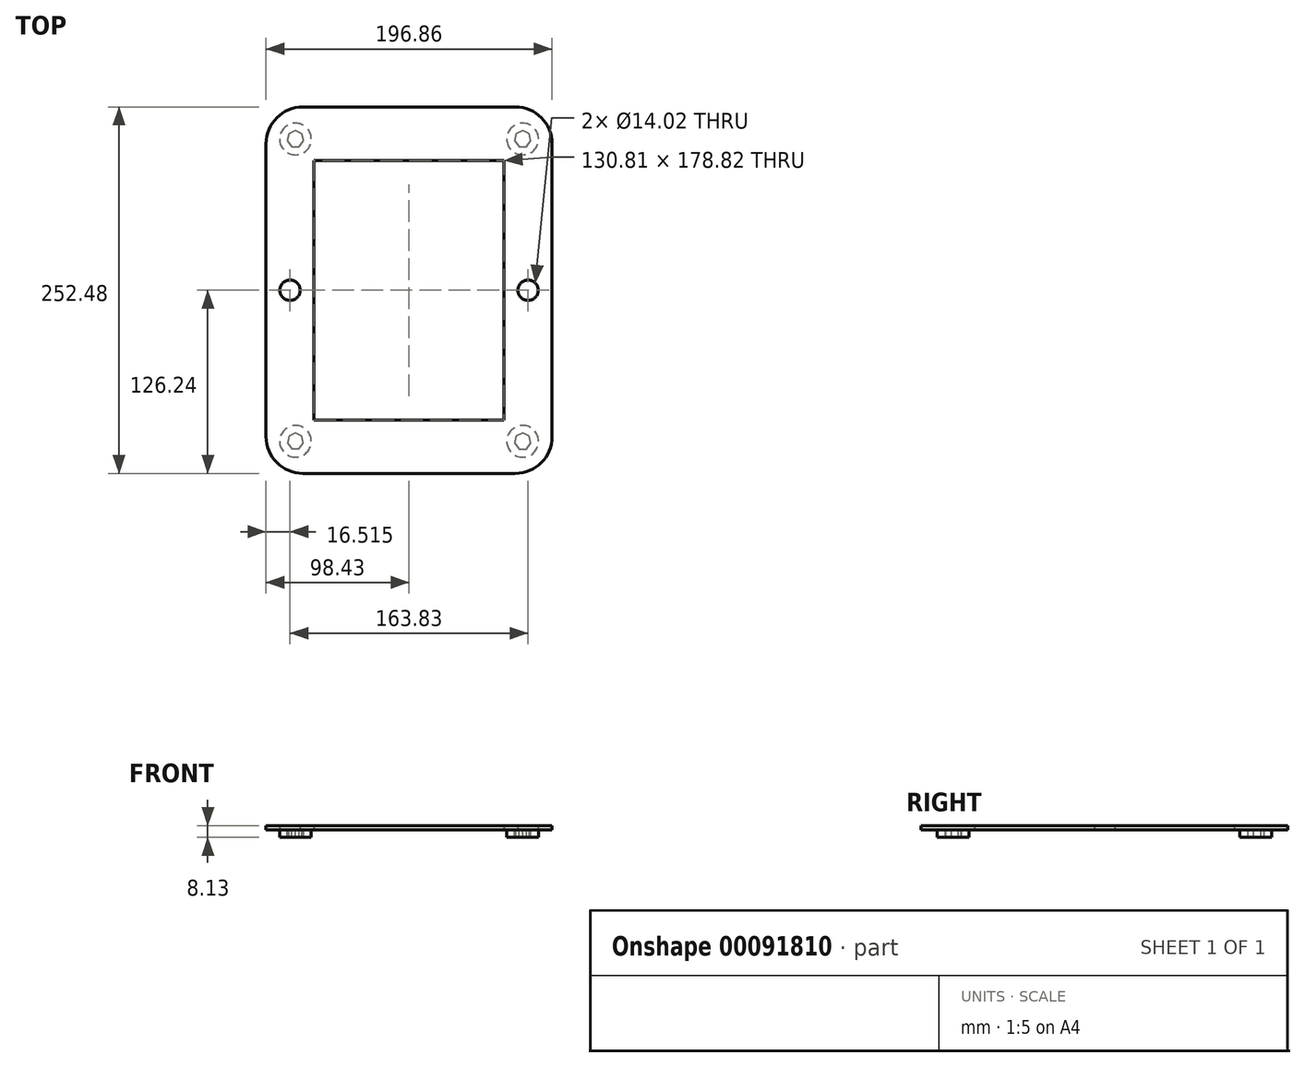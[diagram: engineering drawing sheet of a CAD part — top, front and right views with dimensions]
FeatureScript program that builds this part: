
annotation { "Feature Type Name" : "Feature", "Feature Type Description" : "" }
export const myFeature = defineFeature(function(context is Context, id is Id, definition is map)
    precondition{}
    {
        {
            var Q0;
            Q0=qCreatedBy(makeId("Top.planeOp"),FACE);
            var sketch = newSketch(context, id + "F0", { "sketchPlane" : qUnion([Q0])});
            skLineSegment(sketch, "E0.bottom", {"start": v(-73.02, -126.24) * mm, "end": v(73.03, -126.24) * mm});
            skLineSegment(sketch, "E0.top", {"start": v(-73.03, 126.24) * mm, "end": v(73.02, 126.24) * mm});
            skLineSegment(sketch, "E0.left", {"start": v(-98.42, -100.84) * mm, "end": v(-98.43, 100.84) * mm});
            skLineSegment(sketch, "E0.right", {"start": v(98.43, -100.84) * mm, "end": v(98.42, 100.84) * mm});
            skPoint(sketch, "E0.middle", {"position": v(0, 0) * mm});
            skPoint(sketch, "E1.visualSharp", {"position": v(-98.42, -126.24) * mm});
            skArc(sketch, "E1.filletArc", {"start": v(-98.42, -100.84) * mm, "mid": v(-90.99, -118.8) * mm, "end": v(-73.02, -126.24) * mm});
            skPoint(sketch, "E2.visualSharp", {"position": v(98.43, -126.24) * mm});
            skArc(sketch, "E2.filletArc", {"start": v(73.03, -126.24) * mm, "mid": v(90.99, -118.8) * mm, "end": v(98.43, -100.84) * mm});
            skPoint(sketch, "E3.visualSharp", {"position": v(98.42, 126.24) * mm});
            skArc(sketch, "E3.filletArc", {"start": v(98.42, 100.84) * mm, "mid": v(90.99, 118.8) * mm, "end": v(73.02, 126.24) * mm});
            skPoint(sketch, "E4.visualSharp", {"position": v(-98.43, 126.24) * mm});
            skArc(sketch, "E4.filletArc", {"start": v(-73.03, 126.24) * mm, "mid": v(-90.99, 118.8) * mm, "end": v(-98.43, 100.84) * mm});
            skSolve(sketch);
        }
        {
            var Q0;
            Q0=makeQuery(id+"F0.imprint","IMPRINT",FACE,{"disambiguationData":[TD([[makeQuery(id+"F0.imprint","IMPRINT",EDGE,{"derivedFrom":sQuery(id+"F0.wireOp",EDGE,"E0.bottom")}),1.0]])]});
            extrude(context, id + "F1", {"entities" : qUnion([Q0]), "depth" : 3.05 * mm});
        }
        {
            var Q0;
            Q0=makeQuery(id+"F1.opExtrude","CAP_FACE",FACE,{"disambiguationData":[OSD([sQuery(id+"F0.wireOp",EDGE,"E0.bottom"),sQuery(id+"F0.wireOp",EDGE,"E0.top"),sQuery(id+"F0.wireOp",EDGE,"E0.left"),sQuery(id+"F0.wireOp",EDGE,"E0.right")])],"isStart":true});
            var sketch = newSketch(context, id + "F2", { "sketchPlane" : qUnion([Q0])});
            skLineSegment(sketch, "E5.bottom", {"start": v(-65.4, 89.4) * mm, "end": v(65.4, 89.4) * mm});
            skLineSegment(sketch, "E5.top", {"start": v(-65.4, -89.4) * mm, "end": v(65.4, -89.4) * mm});
            skLineSegment(sketch, "E5.left", {"start": v(-65.4, 89.4) * mm, "end": v(-65.4, -89.4) * mm});
            skLineSegment(sketch, "E5.right", {"start": v(65.4, 89.4) * mm, "end": v(65.4, -89.4) * mm});
            skPoint(sketch, "E5.middle", {"position": v(0, 0) * mm});
            skSolve(sketch);
        }
        {
            var Q0;
            Q0=makeQuery(id+"F2.imprint","IMPRINT",FACE,{"disambiguationData":[TD([[makeQuery(id+"F2.imprint","IMPRINT",EDGE,{"derivedFrom":sQuery(id+"F2.wireOp",EDGE,"E5.bottom")}),-1.0]])]});
            extrude(context, id + "F3", {"entities" : qUnion([Q0]), "operationType" : NewBodyOperationType.REMOVE, "oppositeDirection" : true, "depth" : 25.4 * mm});
        }
        {
            var Q0;
            Q0=makeQuery(id+"F1.opExtrude","CAP_FACE",FACE,{"disambiguationData":[OSD([sQuery(id+"F0.wireOp",EDGE,"E0.bottom"),sQuery(id+"F0.wireOp",EDGE,"E0.top"),sQuery(id+"F0.wireOp",EDGE,"E0.left"),sQuery(id+"F0.wireOp",EDGE,"E0.right")])],"isStart":true});
            var sketch = newSketch(context, id + "F4", { "sketchPlane" : qUnion([Q0])});
            skCircle(sketch, "E6", {"center": v(-81.92, 0) * mm, "radius": 7.01 * mm});
            skCircle(sketch, "E7", {"center": v(81.92, 0) * mm, "radius": 7.01 * mm});
            skPoint(sketch, "E7.centerSnap0", {"position": v(65.4, 0) * mm});
            skSolve(sketch);
        }
        {
            var Q0;
            Q0 = qSketchRegion(id + "F4", true);
            extrude(context, id + "F5", {"entities" : qUnion([Q0]), "operationType" : NewBodyOperationType.REMOVE, "oppositeDirection" : true, "depth" : 25.4 * mm});
        }
        {
            var Q0;
            Q0=makeQuery(id+"F1.opExtrude","CAP_FACE",FACE,{"disambiguationData":[OSD([sQuery(id+"F0.wireOp",EDGE,"E0.bottom"),sQuery(id+"F0.wireOp",EDGE,"E0.top"),sQuery(id+"F0.wireOp",EDGE,"E0.left"),sQuery(id+"F0.wireOp",EDGE,"E0.right"),sQuery(id+"F0.wireOp",EDGE,"E1.filletArc"),sQuery(id+"F0.wireOp",EDGE,"E2.filletArc"),sQuery(id+"F0.wireOp",EDGE,"E3.filletArc"),sQuery(id+"F0.wireOp",EDGE,"E4.filletArc")])],"isStart":true});
            var sketch = newSketch(context, id + "F6", { "sketchPlane" : qUnion([Q0])});
            skCircle(sketch, "E8", {"center": v(78.2, 104.1) * mm, "radius": 10.91 * mm});
            skCircle(sketch, "E9", {"center": v(-78.2, -104.1) * mm, "radius": 10.91 * mm});
            skCircle(sketch, "E10", {"center": v(78.2, -104.1) * mm, "radius": 10.91 * mm});
            skCircle(sketch, "E11.cCircle", {"center": v(78.2, 104.1) * mm, "radius": 5.22 * mm, "construction": true});
            skLineSegment(sketch, "E11.0", {"start": v(75.68, 109.33) * mm, "end": v(80.71, 109.33) * mm});
            skLineSegment(sketch, "E11.1", {"start": v(80.71, 109.33) * mm, "end": v(83.85, 105.4) * mm});
            skLineSegment(sketch, "E11.2", {"start": v(83.85, 105.4) * mm, "end": v(82.73, 100.49) * mm});
            skLineSegment(sketch, "E11.3", {"start": v(82.73, 100.49) * mm, "end": v(78.2, 98.3) * mm});
            skLineSegment(sketch, "E11.4", {"start": v(78.2, 98.3) * mm, "end": v(73.66, 100.49) * mm});
            skLineSegment(sketch, "E11.5", {"start": v(73.66, 100.49) * mm, "end": v(72.54, 105.4) * mm});
            skLineSegment(sketch, "E11.6", {"start": v(72.54, 105.4) * mm, "end": v(75.68, 109.33) * mm});
            skPoint(sketch, "E11.0.midPoint", {"position": v(78.2, 109.33) * mm});
            skCircle(sketch, "E12.cCircle", {"center": v(-78.2, -104.1) * mm, "radius": 5.22 * mm, "construction": true});
            skLineSegment(sketch, "E12.0", {"start": v(-80.71, -98.88) * mm, "end": v(-75.68, -98.88) * mm});
            skLineSegment(sketch, "E12.1", {"start": v(-75.68, -98.88) * mm, "end": v(-72.54, -102.81) * mm});
            skLineSegment(sketch, "E12.2", {"start": v(-72.54, -102.81) * mm, "end": v(-73.66, -107.72) * mm});
            skLineSegment(sketch, "E12.3", {"start": v(-73.66, -107.72) * mm, "end": v(-78.2, -109.9) * mm});
            skLineSegment(sketch, "E12.4", {"start": v(-78.2, -109.9) * mm, "end": v(-82.73, -107.72) * mm});
            skLineSegment(sketch, "E12.5", {"start": v(-82.73, -107.72) * mm, "end": v(-83.85, -102.81) * mm});
            skLineSegment(sketch, "E12.6", {"start": v(-83.85, -102.81) * mm, "end": v(-80.71, -98.88) * mm});
            skPoint(sketch, "E12.0.midPoint", {"position": v(-78.2, -98.88) * mm});
            skCircle(sketch, "E13.cCircle", {"center": v(78.2, -104.1) * mm, "radius": 5.22 * mm, "construction": true});
            skLineSegment(sketch, "E13.0", {"start": v(75.68, -98.88) * mm, "end": v(80.71, -98.88) * mm});
            skLineSegment(sketch, "E13.1", {"start": v(80.71, -98.88) * mm, "end": v(83.85, -102.81) * mm});
            skLineSegment(sketch, "E13.2", {"start": v(83.85, -102.81) * mm, "end": v(82.73, -107.72) * mm});
            skLineSegment(sketch, "E13.3", {"start": v(82.73, -107.72) * mm, "end": v(78.2, -109.9) * mm});
            skLineSegment(sketch, "E13.4", {"start": v(78.2, -109.9) * mm, "end": v(73.66, -107.72) * mm});
            skLineSegment(sketch, "E13.5", {"start": v(73.66, -107.72) * mm, "end": v(72.54, -102.81) * mm});
            skLineSegment(sketch, "E13.6", {"start": v(72.54, -102.81) * mm, "end": v(75.68, -98.88) * mm});
            skPoint(sketch, "E13.0.midPoint", {"position": v(78.2, -98.88) * mm});
            skCircle(sketch, "E14", {"center": v(-78.2, 104.1) * mm, "radius": 10.91 * mm});
            skCircle(sketch, "E15.cCircle", {"center": v(-78.2, 104.1) * mm, "radius": 5.04 * mm, "construction": true});
            skLineSegment(sketch, "E15.0", {"start": v(-80.62, 109.15) * mm, "end": v(-75.77, 109.15) * mm});
            skLineSegment(sketch, "E15.1", {"start": v(-75.77, 109.15) * mm, "end": v(-72.74, 105.35) * mm});
            skLineSegment(sketch, "E15.2", {"start": v(-72.74, 105.35) * mm, "end": v(-73.82, 100.61) * mm});
            skLineSegment(sketch, "E15.3", {"start": v(-73.82, 100.61) * mm, "end": v(-78.2, 98.5) * mm});
            skLineSegment(sketch, "E15.4", {"start": v(-78.2, 98.5) * mm, "end": v(-82.57, 100.61) * mm});
            skLineSegment(sketch, "E15.5", {"start": v(-82.57, 100.61) * mm, "end": v(-83.65, 105.35) * mm});
            skLineSegment(sketch, "E15.6", {"start": v(-83.65, 105.35) * mm, "end": v(-80.62, 109.15) * mm});
            skPoint(sketch, "E15.0.midPoint", {"position": v(-78.2, 109.15) * mm});
            skSolve(sketch);
        }
        {
            var Q0;
            Q0=makeQuery(id+"F6.imprint","IMPRINT",FACE,{"disambiguationData":[TD([[makeQuery(id+"F6.imprint","IMPRINT",EDGE,{"derivedFrom":sQuery(id+"F6.wireOp",EDGE,"E8")}),1.0]])]});
            var Q1;
            Q1=makeQuery(id+"F6.imprint","IMPRINT",FACE,{"disambiguationData":[TD([[makeQuery(id+"F6.imprint","IMPRINT",EDGE,{"derivedFrom":sQuery(id+"F6.wireOp",EDGE,"E14")}),1.0]])]});
            var Q2;
            Q2=makeQuery(id+"F6.imprint","IMPRINT",FACE,{"disambiguationData":[TD([[makeQuery(id+"F6.imprint","IMPRINT",EDGE,{"derivedFrom":sQuery(id+"F6.wireOp",EDGE,"E9")}),1.0]])]});
            var Q3;
            Q3=makeQuery(id+"F6.imprint","IMPRINT",FACE,{"disambiguationData":[TD([[makeQuery(id+"F6.imprint","IMPRINT",EDGE,{"derivedFrom":sQuery(id+"F6.wireOp",EDGE,"E10")}),1.0]])]});
            extrude(context, id + "F7", {"entities" : qUnion([Q0, Q1, Q2, Q3]), "operationType" : NewBodyOperationType.ADD, "depth" : 5.08 * mm});
        }
    });
